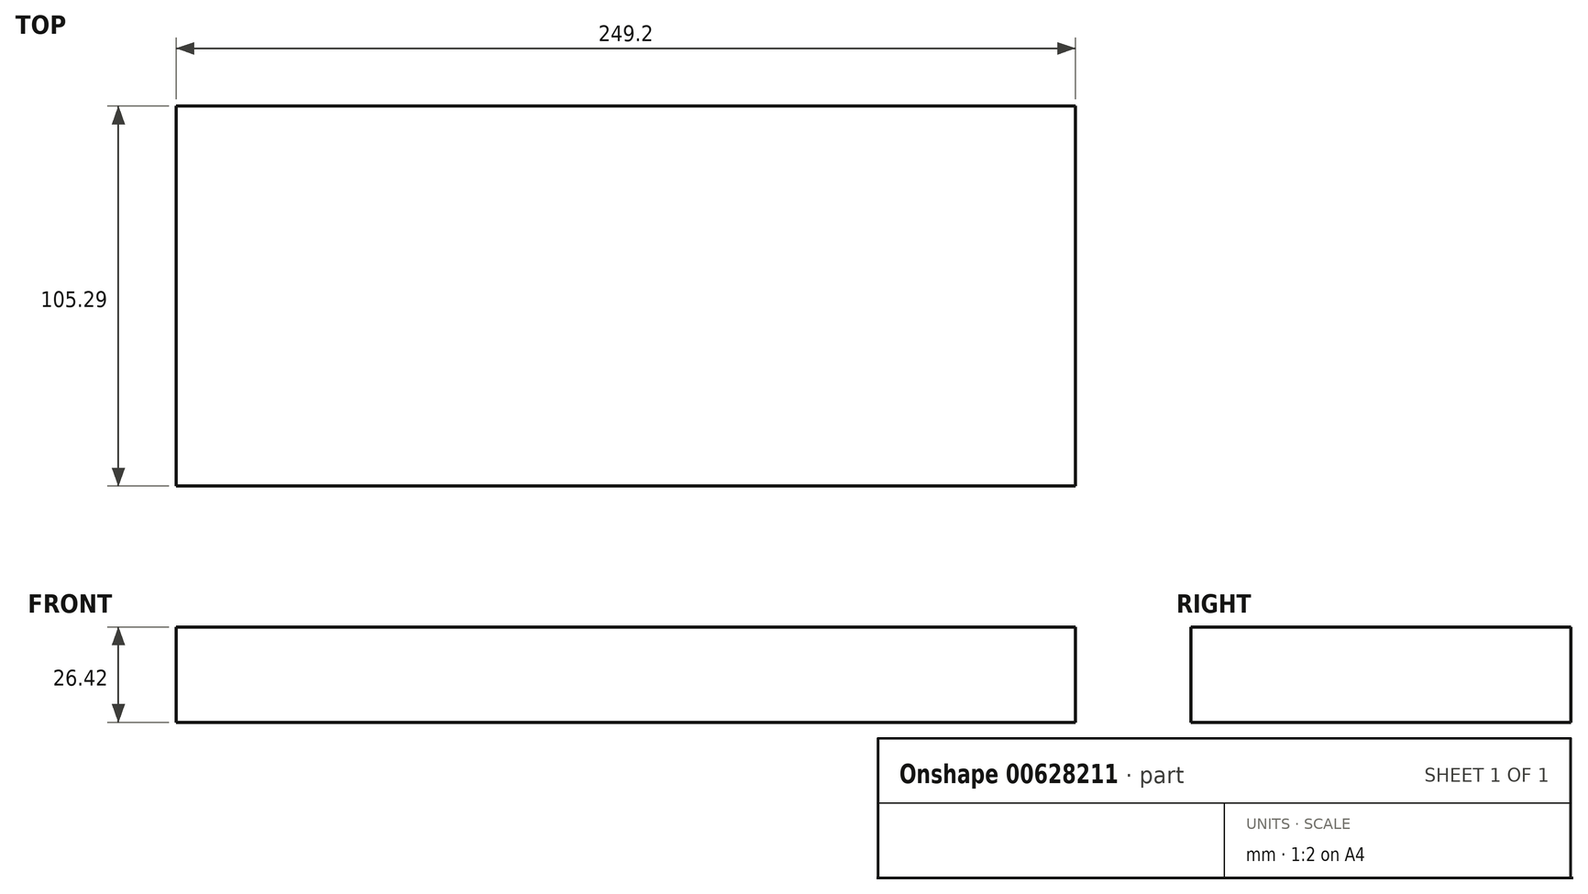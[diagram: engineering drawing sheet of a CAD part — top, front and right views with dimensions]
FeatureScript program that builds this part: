
annotation { "Feature Type Name" : "Feature", "Feature Type Description" : "" }
export const myFeature = defineFeature(function(context is Context, id is Id, definition is map)
    precondition{}
    {
        {
            var Q0;
            Q0=qCreatedBy(makeId("Top.planeOp"),FACE);
            var sketch = newSketch(context, id + "F0", { "sketchPlane" : qUnion([Q0])});
            skLineSegment(sketch, "E0.bottom", {"start": v(-121.84, 46.52) * mm, "end": v(127.36, 46.52) * mm});
            skLineSegment(sketch, "E0.top", {"start": v(-121.84, -58.77) * mm, "end": v(127.36, -58.77) * mm});
            skLineSegment(sketch, "E0.left", {"start": v(-121.84, 46.52) * mm, "end": v(-121.84, -58.77) * mm});
            skLineSegment(sketch, "E0.right", {"start": v(127.36, 46.52) * mm, "end": v(127.36, -58.77) * mm});
            skSolve(sketch);
        }
        {
            var Q0;
            Q0 = qSketchRegion(id + "F0", true);
            extrude(context, id + "F1", {"entities" : qUnion([Q0]), "depth" : 26.42 * mm, "offsetDistance" : 25.4 * mm});
        }
    });
